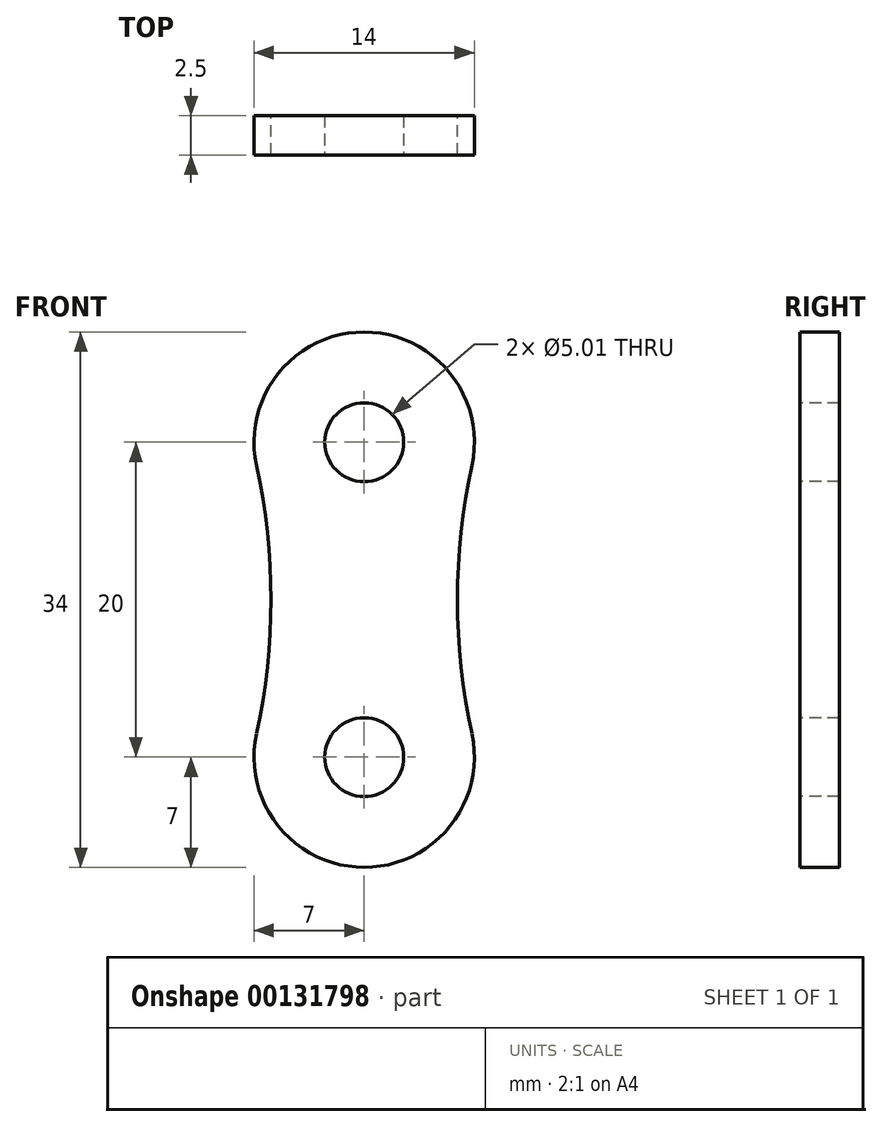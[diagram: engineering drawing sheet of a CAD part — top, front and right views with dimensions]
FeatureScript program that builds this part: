
annotation { "Feature Type Name" : "Feature", "Feature Type Description" : "" }
export const myFeature = defineFeature(function(context is Context, id is Id, definition is map)
    precondition{}
    {
        {
            var Q0;
            Q0=qCreatedBy(makeId("Front.planeOp"),FACE);
            var sketch = newSketch(context, id + "F0", { "sketchPlane" : qUnion([Q0])});
            skArc(sketch, "E0", {"start": v(6.84, 8.51) * mm, "mid": v(0, 17) * mm, "end": v(-6.84, 8.51) * mm});
            skArc(sketch, "E1", {"start": v(-6.84, -8.51) * mm, "mid": v(0, -17) * mm, "end": v(6.84, -8.51) * mm});
            skArc(sketch, "E2", {"start": v(-6.84, -8.51) * mm, "mid": v(-5.92, 0) * mm, "end": v(-6.84, 8.51) * mm});
            skArc(sketch, "E3", {"start": v(6.84, 8.51) * mm, "mid": v(5.92, 0) * mm, "end": v(6.84, -8.51) * mm});
            skSolve(sketch);
        }
        {
            var Q0;
            Q0 = qSketchRegion(id + "F0", true);
            extrude(context, id + "F1", {"entities" : qUnion([Q0]), "depth" : 2.5 * mm});
        }
        {
            var Q0;
            Q0=makeQuery(id+"F1.opExtrude","CAP_FACE",FACE,{"disambiguationData":[OSD([sQuery(id+"F0.wireOp",EDGE,"E0"),sQuery(id+"F0.wireOp",EDGE,"E1"),sQuery(id+"F0.wireOp",EDGE,"E2"),sQuery(id+"F0.wireOp",EDGE,"E3")])],"isStart":false});
            var sketch = newSketch(context, id + "F2", { "sketchPlane" : qUnion([Q0])});
            skCircle(sketch, "E4", {"center": v(0, 10) * mm, "radius": 2.5 * mm});
            skCircle(sketch, "E5", {"center": v(0, -10) * mm, "radius": 2.5 * mm});
            skSolve(sketch);
        }
        {
            var Q0;
            Q0=makeQuery(id+"F2.imprint","IMPRINT",FACE,{"disambiguationData":[TD([[makeQuery(id+"F2.imprint","IMPRINT",EDGE,{"derivedFrom":sQuery(id+"F2.wireOp",EDGE,"E4")}),1.0]])]});
            var Q1;
            Q1=makeQuery(id+"F2.imprint","IMPRINT",FACE,{"disambiguationData":[TD([[makeQuery(id+"F2.imprint","IMPRINT",EDGE,{"derivedFrom":sQuery(id+"F2.wireOp",EDGE,"E5")}),1.0]])]});
            extrude(context, id + "F3", {"entities" : qUnion([Q0, Q1]), "operationType" : NewBodyOperationType.REMOVE, "oppositeDirection" : true, "depth" : 25 * mm});
        }
    });
